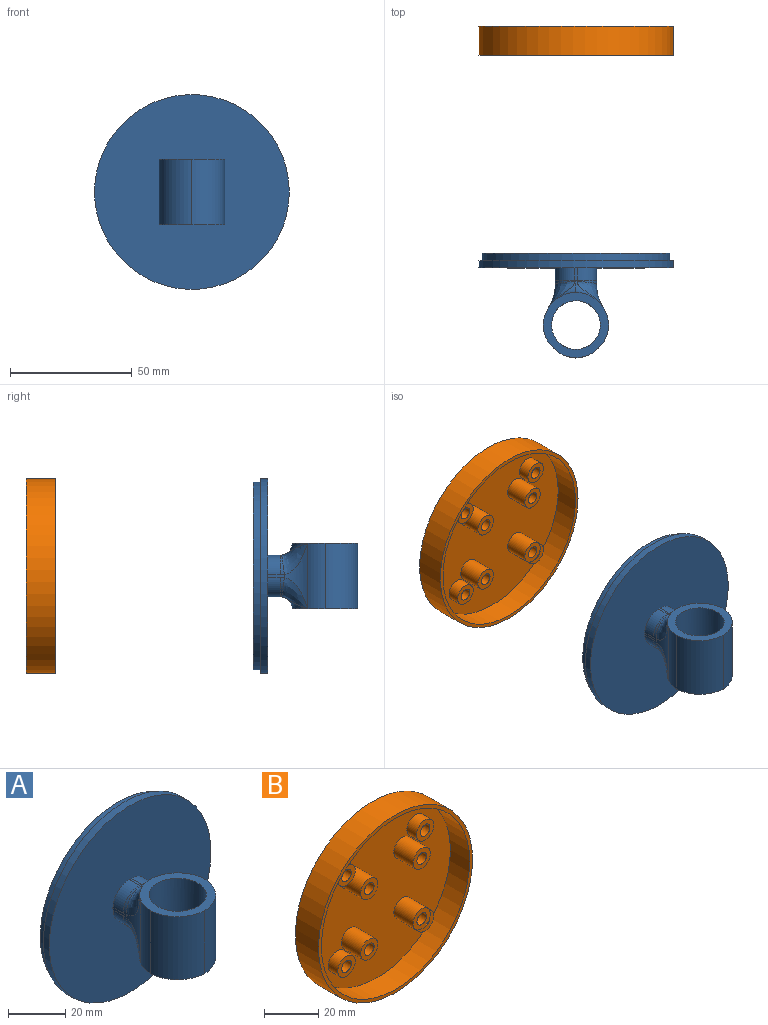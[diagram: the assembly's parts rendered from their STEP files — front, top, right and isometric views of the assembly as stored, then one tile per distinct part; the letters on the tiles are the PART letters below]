
ASSEMBLY  parts=2 mates=1
PART A: 36 faces, bbox 80x43x80 mm
  f0: plane 80x80mm, normal (0,-1,0), area 4792.5mm2, adj f5,f7,f8,f9,f10,f24,f27,f30
  f1: cylinder r=37mm len=74mm, axis (0,-1,0), area 697.4mm2, adj f3,f6
  f2: cylinder r=38.5mm len=77mm, axis (0,-1,0), area 725.7mm2, adj f3,f4
  f3: plane 77x77mm, normal (0,1,0), area 355.8mm2, adj f1,f2
  f4: plane 80x80mm, normal (0,1,0), area 369.9mm2, adj f2,f5
  f5: cylinder r=40mm len=80mm, axis (0,1,0), area 754mm2, adj f0,f4
  f6: plane 74x74mm, normal (0,1,0), area 4300.8mm2, adj f1
  f7: plane 5.03x1mm, normal (0,0,-1), area 5mm2, adj f0,f22,f23,f24,f33
  f8: plane 6.83x1.25mm, normal (1,0,0), area 7mm2, adj f0,f19,f24,f25,f27,f28
  f9: plane 5.03x1mm, normal (0,0,1), area 5mm2, adj f0,f20,f21,f27,f30
  f10: plane 6.83x1.25mm, normal (-1,0,0), area 7mm2, adj f0,f18,f30,f31,f33,f34
  f11: plane 26.98x26.98mm, normal (0,0,-1), area 246.6mm2, adj f13,f14,f15,f16,f17,f22,f23
  f12: plane 26.98x26.98mm, normal (0,0,1), area 246.6mm2, adj f13,f14,f15,f16,f17,f20,f21
  f13: cylinder r=10mm len=27mm, axis (0,0,-1), area 1696.5mm2, adj f11,f12
  f14: cylinder r=14mm len=27mm, axis (0,0,1), area 566.8mm2, adj f11,f12,f15,f16
  f15: cylinder r=14mm len=27mm, axis (0,0,-1), area 200.7mm2, adj f11,f12,f14,f18
  f16: cylinder r=14mm len=27mm, axis (0,0,-1), area 566.8mm2, adj f11,f12,f14,f17
  f17: cylinder r=14mm len=27mm, axis (0,0,1), area 200.7mm2, adj f11,f12,f16,f19
  f18: cylinder r=18mm len=27mm, axis (0,0,-1), area 103.1mm2, adj f10,f15,f32,f35
  f19: cylinder r=18mm len=27mm, axis (0,0,1), area 103.1mm2, adj f8,f17,f26,f29
  f20: torus R=19mm, axis (0,0,-1), area 34.1mm2, adj f9,f12,f21,f28,f29
  f21: torus R=19mm, axis (0,0,-1), area 34.1mm2, adj f9,f12,f20,f31,f32
  f22: torus R=19mm, axis (0,0,-1), area 34.1mm2, adj f7,f11,f23,f25,f26
  f23: torus R=19mm, axis (0,0,-1), area 34.1mm2, adj f7,f11,f22,f34,f35
  f24: cylinder r=8mm len=8mm, axis (0,1,0), area 63.2mm2, adj f0,f7,f8,f25
  f25: bspline ~8.23x8.09mm, area 13.8mm2, adj f8,f22,f24,f26
  f26: bspline ~13x11.59mm, area 97.8mm2, adj f19,f22,f25
  f27: cylinder r=8mm len=8mm, axis (0,-1,0), area 63.2mm2, adj f0,f8,f9,f28
  f28: bspline ~8.32x8.09mm, area 13.8mm2, adj f8,f20,f27,f29
  f29: bspline ~13x11.33mm, area 97.8mm2, adj f19,f20,f28
  f30: cylinder r=8mm len=8mm, axis (0,1,0), area 63.2mm2, adj f0,f9,f10,f31
  f31: bspline ~8.32x8.09mm, area 13.8mm2, adj f10,f21,f30,f32
  f32: bspline ~13x11.59mm, area 97.8mm2, adj f18,f21,f31
  f33: cylinder r=8mm len=8mm, axis (0,-1,0), area 63.2mm2, adj f0,f7,f10,f34
  f34: bspline ~8.23x8.09mm, area 13.8mm2, adj f10,f23,f33,f35
  f35: bspline ~13x11.33mm, area 97.8mm2, adj f18,f23,f34
PART B: 37 faces, bbox 80x12x80 mm
  f0: cylinder r=40mm len=80mm, axis (0,1,0), area 3015.9mm2, adj f1,f3
  f1: plane 80x80mm, normal (0,1,0), area 5026.5mm2, adj f0
  f2: cylinder r=38.5mm len=77mm, axis (0,1,0), area 2419mm2, adj f3,f4
  f3: plane 80x80mm, normal (0,-1,0), area 369.9mm2, adj f0,f2
  f4: plane 77x77mm, normal (0,-1,0), area 4147.7mm2, adj f2,f6,f9,f14,f17,f22,f25,f29
  f5: cylinder r=2.5mm len=5mm, axis (0,1,0), area 78.5mm2, adj f7,f8
  f6: cylinder r=4.5mm len=9mm, axis (0,1,0), area 141.4mm2, adj f4,f7
  f7: plane 9x9mm, normal (0,-1,0), area 44mm2, adj f5,f6
  f8: plane 5x5mm, normal (0,-1,0), area 19.6mm2, adj f5
  f9: cylinder r=4.5mm len=9mm, axis (0,1,0), area 141.4mm2, adj f4,f11
  f10: cylinder r=2.5mm len=5mm, axis (0,1,0), area 78.5mm2, adj f11,f12
  f11: plane 9x9mm, normal (0,-1,0), area 44mm2, adj f9,f10
  f12: plane 5x5mm, normal (0,-1,0), area 19.6mm2, adj f10
  f13: cylinder r=2.5mm len=5mm, axis (0,1,0), area 78.5mm2, adj f15,f16
  f14: cylinder r=4.5mm len=9mm, axis (0,1,0), area 141.4mm2, adj f4,f15
  f15: plane 9x9mm, normal (0,-1,0), area 44mm2, adj f13,f14
  f16: plane 5x5mm, normal (0,-1,0), area 19.6mm2, adj f13
  f17: cylinder r=4.5mm len=9mm, axis (0,1,0), area 141.4mm2, adj f4,f19
  f18: cylinder r=2.5mm len=5mm, axis (0,1,0), area 78.5mm2, adj f19,f20
  f19: plane 9x9mm, normal (0,-1,0), area 44mm2, adj f17,f18
  f20: plane 5x5mm, normal (0,-1,0), area 19.6mm2, adj f18
  f21: cylinder r=2.5mm len=10mm, axis (0,1,0), area 157.1mm2, adj f23,f24
  f22: cylinder r=4.5mm len=10mm, axis (0,1,0), area 282.7mm2, adj f4,f23
  f23: plane 9x9mm, normal (0,-1,0), area 44mm2, adj f21,f22
  f24: plane 5x5mm, normal (0,-1,0), area 19.6mm2, adj f21
  f25: cylinder r=4.5mm len=10mm, axis (0,1,0), area 282.7mm2, adj f4,f27
  f26: cylinder r=2.5mm len=10mm, axis (0,1,0), area 157.1mm2, adj f27,f28
  f27: plane 9x9mm, normal (0,-1,0), area 44mm2, adj f25,f26
  f28: plane 5x5mm, normal (0,-1,0), area 19.6mm2, adj f26
  f29: cylinder r=4.5mm len=10mm, axis (0,1,0), area 282.7mm2, adj f4,f31
  f30: cylinder r=2.5mm len=10mm, axis (0,1,0), area 157.1mm2, adj f31,f32
  f31: plane 9x9mm, normal (0,-1,0), area 44mm2, adj f29,f30
  f32: plane 5x5mm, normal (0,-1,0), area 19.6mm2, adj f30
  f33: cylinder r=2.5mm len=10mm, axis (0,1,0), area 157.1mm2, adj f35,f36
  f34: cylinder r=4.5mm len=10mm, axis (0,1,0), area 282.7mm2, adj f4,f35
  f35: plane 9x9mm, normal (0,-1,0), area 44mm2, adj f33,f34
  f36: plane 5x5mm, normal (0,-1,0), area 19.6mm2, adj f33
PLACE A t=(-81.57,-104.15,-14.52)mm
PLACE B t=(-81.57,-19.87,-14.52)mm fixed
MATE slider B.f0 <-> A.f1  axis (0,1,0) through (-81.57,-19.87,-14.52)mm
